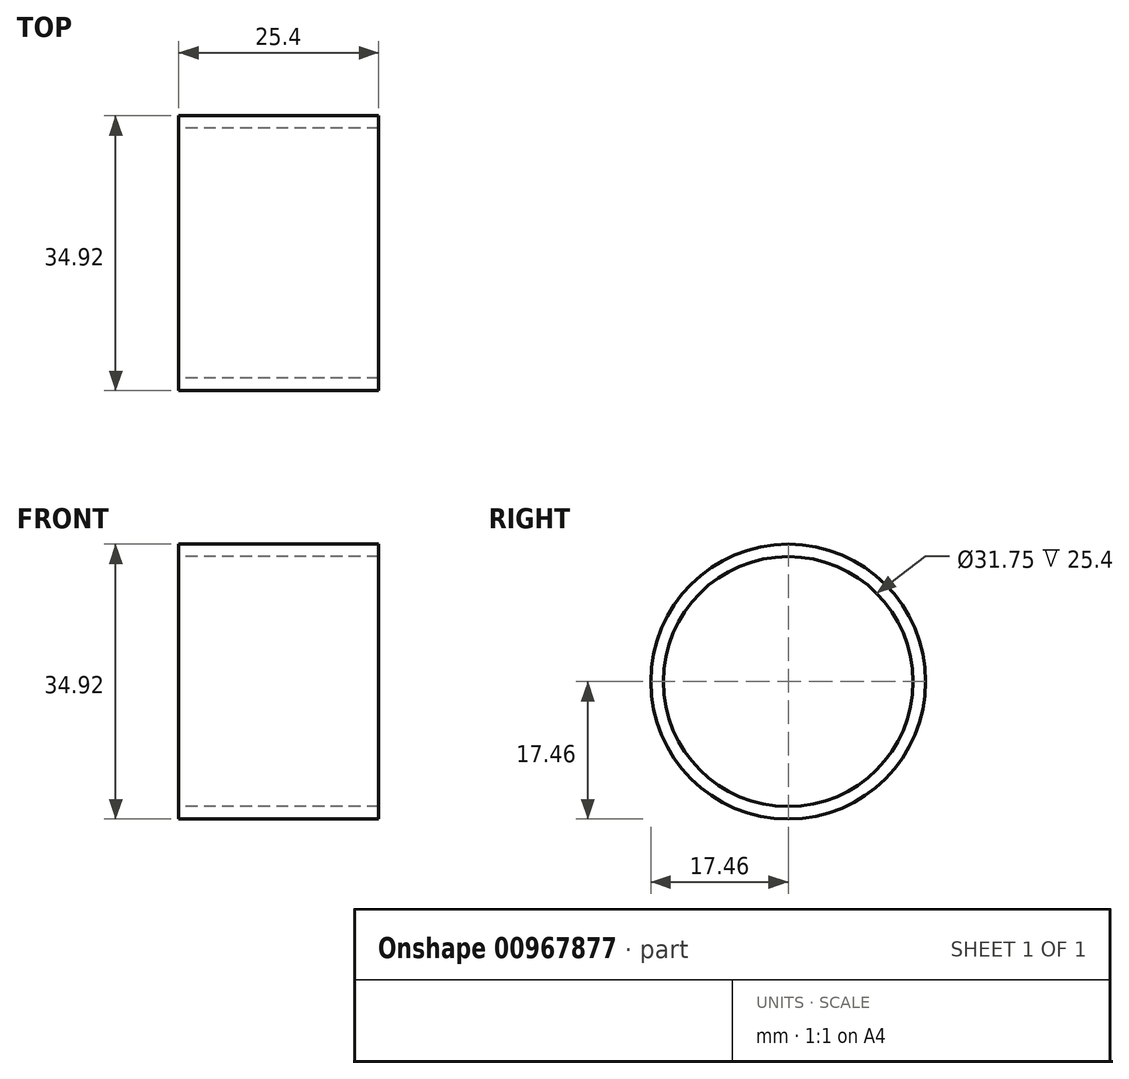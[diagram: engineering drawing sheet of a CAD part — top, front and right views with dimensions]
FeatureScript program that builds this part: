
annotation { "Feature Type Name" : "Feature", "Feature Type Description" : "" }
export const myFeature = defineFeature(function(context is Context, id is Id, definition is map)
    precondition{}
    {
        {
            var Q0;
            Q0=qCreatedBy(makeId("Right.planeOp"),FACE);
            var sketch = newSketch(context, id + "F0", { "sketchPlane" : qUnion([Q0])});
            skCircle(sketch, "E0", {"center": v(0, 0) * mm, "radius": 17.46 * mm});
            skCircle(sketch, "E1", {"center": v(0, 0) * mm, "radius": 15.88 * mm});
            skPoint(sketch, "E2", {"position": v(0, 15.88) * mm});
            skPoint(sketch, "E3", {"position": v(0, 17.46) * mm});
            skSolve(sketch);
        }
        {
            var Q0;
            Q0=makeQuery(id+"F0.imprint","IMPRINT",FACE,{"disambiguationData":[TD([[makeQuery(id+"F0.imprint","IMPRINT",EDGE,{"derivedFrom":sQuery(id+"F0.wireOp",EDGE,"E0")}),1.0]])]});
            extrude(context, id + "F1", {"entities" : qUnion([Q0]), "endBound" : BoundingType.SYMMETRIC, "depth" : 25.4 * mm, "offsetDistance" : 25.4 * mm});
        }
    });
